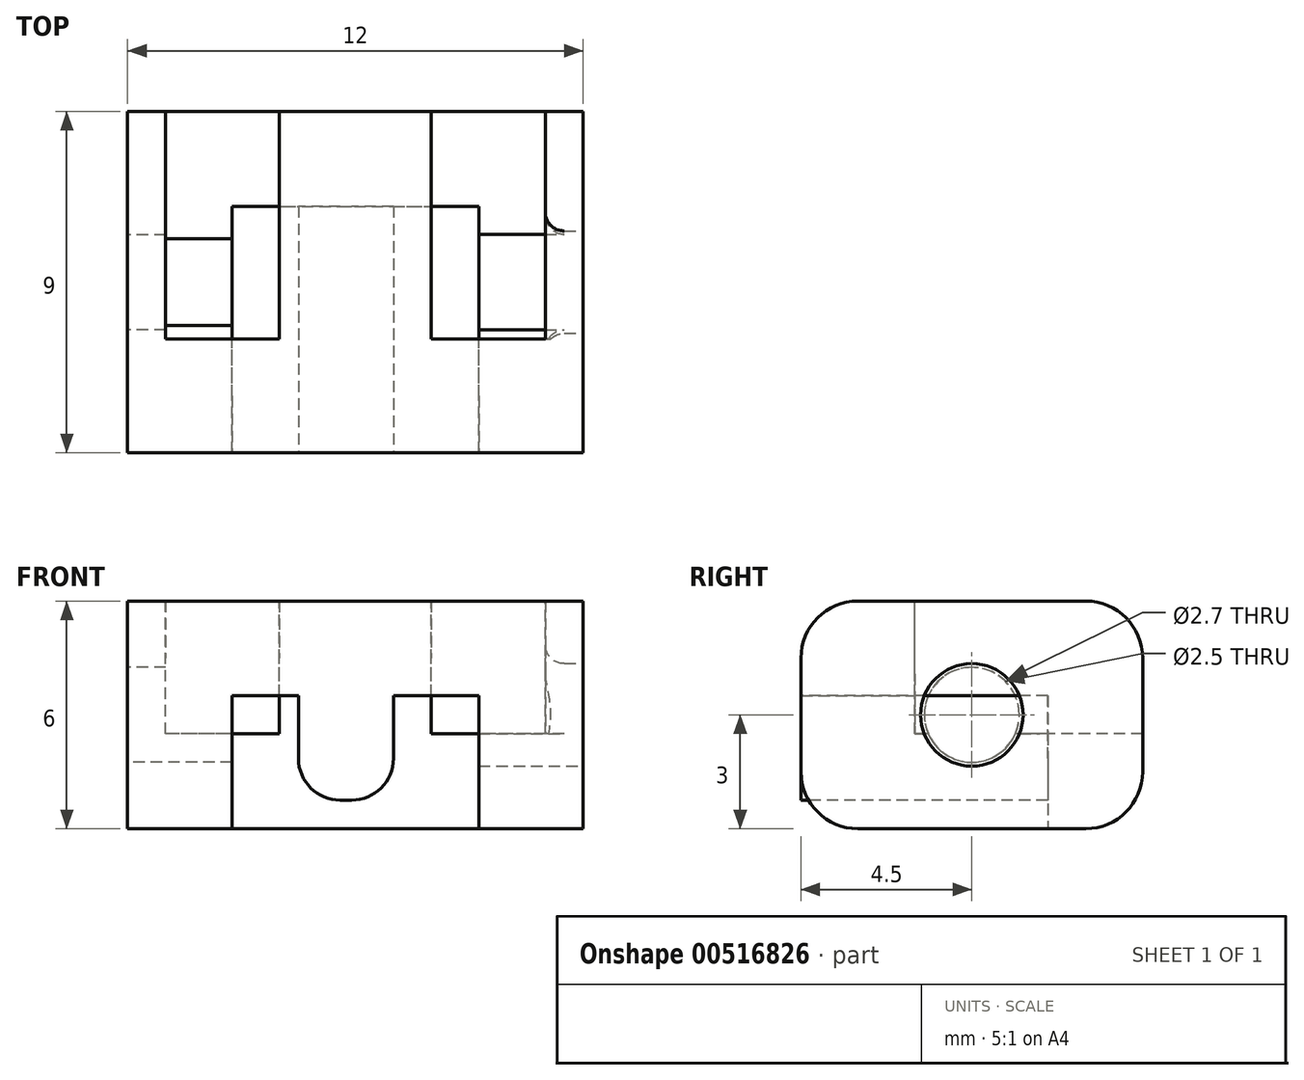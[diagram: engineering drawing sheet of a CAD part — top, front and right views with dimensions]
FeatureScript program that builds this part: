
annotation { "Feature Type Name" : "Feature", "Feature Type Description" : "" }
export const myFeature = defineFeature(function(context is Context, id is Id, definition is map)
    precondition{}
    {
        {
            var Q0;
            Q0=qCreatedBy(makeId("Top.planeOp"),FACE);
            var sketch = newSketch(context, id + "F0", { "sketchPlane" : qUnion([Q0])});
            skLineSegment(sketch, "E0.bottom", {"start": v(6, -4.5) * mm, "end": v(-6, -4.5) * mm});
            skLineSegment(sketch, "E0.top", {"start": v(6, 4.5) * mm, "end": v(-6, 4.5) * mm});
            skLineSegment(sketch, "E0.left", {"start": v(6, -4.5) * mm, "end": v(6, 4.5) * mm});
            skLineSegment(sketch, "E0.right", {"start": v(-6, -4.5) * mm, "end": v(-6, 4.5) * mm});
            skPoint(sketch, "E0.middle", {"position": v(0, 0) * mm});
            skSolve(sketch);
        }
        {
            var Q0;
            Q0=qSketchRegion(id+"F0",true);
            extrude(context, id + "F1", {"entities" : qUnion([Q0]), "depth" : 6 * mm, "offsetDistance" : 25 * mm});
        }
        {
            var Q0;
            Q0=makeQuery(id+"F1.opExtrude","CAP_FACE",FACE,{"disambiguationData":[OSD([sQuery(id+"F0.wireOp",EDGE,"E0.bottom"),sQuery(id+"F0.wireOp",EDGE,"E0.top"),sQuery(id+"F0.wireOp",EDGE,"E0.left"),sQuery(id+"F0.wireOp",EDGE,"E0.right")])],"isStart":false});
            var sketch = newSketch(context, id + "F2", { "sketchPlane" : qUnion([Q0])});
            skLineSegment(sketch, "E1.bottom", {"start": v(-5, 4.5) * mm, "end": v(-2, 4.5) * mm});
            skLineSegment(sketch, "E1.top", {"start": v(-5, -1.5) * mm, "end": v(-2, -1.5) * mm});
            skLineSegment(sketch, "E1.left", {"start": v(-5, 4.5) * mm, "end": v(-5, -1.5) * mm});
            skLineSegment(sketch, "E1.right", {"start": v(-2, 4.5) * mm, "end": v(-2, -1.5) * mm});
            skLineSegment(sketch, "E2.bottom", {"start": v(5, 4.5) * mm, "end": v(2, 4.5) * mm});
            skLineSegment(sketch, "E2.top", {"start": v(5, -1.5) * mm, "end": v(2, -1.5) * mm});
            skLineSegment(sketch, "E2.left", {"start": v(5, 4.5) * mm, "end": v(5, -1.5) * mm});
            skLineSegment(sketch, "E2.right", {"start": v(2, 4.5) * mm, "end": v(2, -1.5) * mm});
            skSolve(sketch);
        }
        {
            var Q0;
            Q0=makeQuery(id+"F2.imprint","IMPRINT",FACE,{"disambiguationData":[TD([[makeQuery(id+"F2.imprint","IMPRINT",EDGE,{"derivedFrom":sQuery(id+"F2.wireOp",EDGE,"E2.bottom")}),1.0]])]});
            var Q1;
            Q1=makeQuery(id+"F2.imprint","IMPRINT",FACE,{"disambiguationData":[TD([[makeQuery(id+"F2.imprint","IMPRINT",EDGE,{"derivedFrom":sQuery(id+"F2.wireOp",EDGE,"E1.bottom")}),1.0]])]});
            extrude(context, id + "F3", {"entities" : qUnion([Q0, Q1]), "operationType" : NewBodyOperationType.REMOVE, "oppositeDirection" : true, "depth" : 3.5 * mm, "offsetDistance" : 25 * mm});
        }
        {
            var Q0;
            Q0=makeQuery(id+"F1.opExtrude","CAP_FACE",FACE,{"disambiguationData":[OSD([sQuery(id+"F0.wireOp",EDGE,"E0.bottom"),sQuery(id+"F0.wireOp",EDGE,"E0.top"),sQuery(id+"F0.wireOp",EDGE,"E0.left"),sQuery(id+"F0.wireOp",EDGE,"E0.right")])],"isStart":true});
            var sketch = newSketch(context, id + "F4", { "sketchPlane" : qUnion([Q0])});
            skLineSegment(sketch, "E3.bottom", {"start": v(-3.25, 4.5) * mm, "end": v(3.25, 4.5) * mm});
            skLineSegment(sketch, "E3.top", {"start": v(-3.25, -2) * mm, "end": v(3.25, -2) * mm});
            skLineSegment(sketch, "E3.left", {"start": v(-3.25, 4.5) * mm, "end": v(-3.25, -2) * mm});
            skLineSegment(sketch, "E3.right", {"start": v(3.25, 4.5) * mm, "end": v(3.25, -2) * mm});
            skSolve(sketch);
        }
        {
            var Q0;
            Q0=qSketchRegion(id+"F4",true);
            extrude(context, id + "F5", {"entities" : qUnion([Q0]), "operationType" : NewBodyOperationType.REMOVE, "oppositeDirection" : true, "depth" : 3.5 * mm, "offsetDistance" : 25 * mm});
        }
        {
            var Q0;
            Q0=makeQuery(id+"F1.opExtrude","SWEPT_FACE",FACE,{"disambiguationData":[OSD([sQuery(id+"F0.wireOp",EDGE,"E0.left")])]});
            var sketch = newSketch(context, id + "F6", { "sketchPlane" : qUnion([Q0])});
            skLineSegment(sketch, "E4", {"start": v(0, 6) * mm, "end": v(0, 0) * mm, "construction": true});
            skLineSegment(sketch, "E5", {"start": v(-4.5, 3) * mm, "end": v(4.5, 3) * mm, "construction": true});
            skCircle(sketch, "E6", {"center": v(0, 3) * mm, "radius": 1.35 * mm});
            skSolve(sketch);
        }
        {
            var Q0;
            Q0=qSketchRegion(id+"F6",true);
            extrude(context, id + "F7", {"entities" : qUnion([Q0]), "operationType" : NewBodyOperationType.REMOVE, "oppositeDirection" : true, "depth" : 3 * mm, "offsetDistance" : 25 * mm});
        }
        {
            var Q0;
            Q0=makeQuery(id+"F1.opExtrude","SWEPT_FACE",FACE,{"disambiguationData":[OSD([sQuery(id+"F0.wireOp",EDGE,"E0.right")])]});
            var sketch = newSketch(context, id + "F8", { "sketchPlane" : qUnion([Q0])});
            skLineSegment(sketch, "E7", {"start": v(-4.5, 3) * mm, "end": v(4.5, 3) * mm, "construction": true});
            skLineSegment(sketch, "E8", {"start": v(0, 6) * mm, "end": v(0, 0) * mm, "construction": true});
            skCircle(sketch, "E9", {"center": v(0, 3) * mm, "radius": 1.25 * mm});
            skSolve(sketch);
        }
        {
            var Q0;
            Q0=qSketchRegion(id+"F8",true);
            extrude(context, id + "F9", {"entities" : qUnion([Q0]), "operationType" : NewBodyOperationType.REMOVE, "endBound" : BoundingType.UP_TO_NEXT, "oppositeDirection" : true, "depth" : 3 * mm, "offsetDistance" : 25 * mm});
        }
        {
            var Q0;
            Q0=makeQuery(id+"F3.boolean.opBoolean","COPY",EDGE,{"derivedFrom":makeQuery(id+"F3.opExtrude","CAP_EDGE",EDGE,{"disambiguationData":[OSD([sQuery(id+"F2.wireOp",EDGE,"E2.right")])],"isStart":true})});
            var Q1;
            Q1=makeQuery(id+"F3.boolean.opBoolean","COPY",EDGE,{"derivedFrom":makeQuery(id+"F3.opExtrude","CAP_EDGE",EDGE,{"disambiguationData":[OSD([sQuery(id+"F2.wireOp",EDGE,"E1.right")])],"isStart":true})});
            var Q2;
            Q2=makeQuery(id+"F1.opExtrude","CAP_EDGE",EDGE,{"disambiguationData":[OSD([sQuery(id+"F0.wireOp",EDGE,"E0.bottom")])],"isStart":false});
            var Q3;
            {var subQ0=sQuery(id+"F0.wireOp",EDGE,"E0.bottom");var subQ1=sQuery(id+"F0.wireOp",EDGE,"E0.right");Q3=makeQuery(id+"F5.boolean.opBoolean","SPLIT",EDGE,{"disambiguationData":[TD([makeQuery(id+"F1.opExtrude","SWEPT_FACE",FACE,{"disambiguationData":[OSD([subQ1])]})])],"derivedFrom":makeQuery(id+"F1.opExtrude","CAP_EDGE",EDGE,{"disambiguationData":[OSD([subQ0])],"isStart":true})});}
            var Q4;
            {var subQ0=sQuery(id+"F0.wireOp",EDGE,"E0.bottom");var subQ1=sQuery(id+"F0.wireOp",EDGE,"E0.left");Q4=makeQuery(id+"F5.boolean.opBoolean","SPLIT",EDGE,{"disambiguationData":[TD([makeQuery(id+"F1.opExtrude","SWEPT_FACE",FACE,{"disambiguationData":[OSD([subQ1])]})])],"derivedFrom":makeQuery(id+"F1.opExtrude","CAP_EDGE",EDGE,{"disambiguationData":[OSD([subQ0])],"isStart":true})});}
            var Q5;
            Q5=makeQuery(id+"F1.opExtrude","CAP_EDGE",EDGE,{"disambiguationData":[OSD([sQuery(id+"F0.wireOp",EDGE,"E0.top")])],"isStart":true});
            var Q6;
            {var subQ0=sQuery(id+"F0.wireOp",EDGE,"E0.right");var subQ1=sQuery(id+"F0.wireOp",EDGE,"E0.top");Q6=makeQuery(id+"F3.boolean.opBoolean","SPLIT",EDGE,{"disambiguationData":[TD([makeQuery(id+"F1.opExtrude","SWEPT_FACE",FACE,{"disambiguationData":[OSD([subQ0])]})])],"derivedFrom":makeQuery(id+"F1.opExtrude","CAP_EDGE",EDGE,{"disambiguationData":[OSD([subQ1])],"isStart":false})});}
            var Q7;
            {var subQ0=sQuery(id+"F0.wireOp",EDGE,"E0.left");var subQ1=sQuery(id+"F0.wireOp",EDGE,"E0.top");Q7=makeQuery(id+"F3.boolean.opBoolean","SPLIT",EDGE,{"disambiguationData":[TD([makeQuery(id+"F1.opExtrude","SWEPT_FACE",FACE,{"disambiguationData":[OSD([subQ0])]})])],"derivedFrom":makeQuery(id+"F1.opExtrude","CAP_EDGE",EDGE,{"disambiguationData":[OSD([subQ1])],"isStart":false})});}
            var Q8;
            {var subQ0=sQuery(id+"F0.wireOp",EDGE,"E0.top");Q8=makeQuery(id+"F3.boolean.opBoolean","SPLIT",EDGE,{"disambiguationData":[TD([makeQuery(id+"F3.opExtrude","SWEPT_FACE",FACE,{"disambiguationData":[OSD([sQuery(id+"F2.wireOp",EDGE,"E1.right")])]})])],"derivedFrom":makeQuery(id+"F1.opExtrude","CAP_EDGE",EDGE,{"disambiguationData":[OSD([subQ0])],"isStart":false})});}
            fillet(context, id + "F10", {"entities" : qUnion([Q0, Q1, Q2, Q3, Q4, Q5, Q6, Q7, Q8]), "radius" : 1.5 * mm, "tangentPropagation" : true, "allowEdgeOverflow" : false});
        }
        {
            var Q0;
            Q0=makeQuery(id+"F5.boolean.opBoolean","COPY",FACE,{"derivedFrom":makeQuery(id+"F5.opExtrude","CAP_FACE",FACE,{"disambiguationData":[OSD([sQuery(id+"F4.wireOp",EDGE,"E3.bottom"),sQuery(id+"F4.wireOp",EDGE,"E3.top"),sQuery(id+"F4.wireOp",EDGE,"E3.left"),sQuery(id+"F4.wireOp",EDGE,"E3.right")])],"isStart":false})});
            var sketch = newSketch(context, id + "F11", { "sketchPlane" : qUnion([Q0])});
            skLineSegment(sketch, "E10.bottom", {"start": v(-1.5, -2) * mm, "end": v(1, -2) * mm});
            skLineSegment(sketch, "E10.top", {"start": v(-1.5, 4.5) * mm, "end": v(1, 4.5) * mm});
            skLineSegment(sketch, "E10.left", {"start": v(-1.5, -2) * mm, "end": v(-1.5, 4.5) * mm});
            skLineSegment(sketch, "E10.right", {"start": v(1, -2) * mm, "end": v(1, 4.5) * mm});
            skSolve(sketch);
        }
        {
            var Q0;
            Q0=qSketchRegion(id+"F11",true);
            extrude(context, id + "F12", {"entities" : qUnion([Q0]), "operationType" : NewBodyOperationType.ADD, "depth" : 2.75 * mm, "offsetDistance" : 25 * mm});
        }
        {
            var Q0;
            Q0=makeQuery(id+"F12.opExtrude","CAP_EDGE",EDGE,{"disambiguationData":[OSD([sQuery(id+"F11.wireOp",EDGE,"E10.left")])],"isStart":false});
            var Q1;
            Q1=makeQuery(id+"F12.opExtrude","CAP_EDGE",EDGE,{"disambiguationData":[OSD([sQuery(id+"F11.wireOp",EDGE,"E10.right")])],"isStart":false});
            fillet(context, id + "F13", {"entities" : qUnion([Q0, Q1]), "radius" : 1.1 * mm, "tangentPropagation" : true, "allowEdgeOverflow" : false});
        }
        {
            var Q0;
            Q0=makeQuery(id+"F7.boolean.opBoolean","COPY",EDGE,{"derivedFrom":makeQuery(id+"F7.opExtrude","CAP_EDGE",EDGE,{"disambiguationData":[OSD([sQuery(id+"F6.wireOp",EDGE,"E6")])],"isStart":true})});
            var Q1;
            Q1=makeQuery(id+"F9.boolean.opBoolean","COPY",EDGE,{"derivedFrom":makeQuery(id+"F9.opExtrude","CAP_EDGE",EDGE,{"disambiguationData":[OSD([sQuery(id+"F8.wireOp",EDGE,"E9")])],"isStart":true})});
            var Q2;
            Q2=makeQuery(id+"F9.boolean.opBoolean","COPY",EDGE,{"derivedFrom":makeQuery(id+"F9.opExtrude","CAP_EDGE",EDGE,{"disambiguationData":[OSD([sQuery(id+"F8.wireOp",EDGE,"E9")]),topologyDisambiguationEdgeConnected([makeQuery(id+"F3.boolean.opBoolean","COPY",FACE,{"derivedFrom":makeQuery(id+"F3.opExtrude","SWEPT_FACE",FACE,{"disambiguationData":[OSD([sQuery(id+"F2.wireOp",EDGE,"E1.left")])]})})])],"isStart":false})});
            var Q3;
            Q3=makeQuery(id+"F7.boolean.opBoolean","INTERSECT",EDGE,{"derivedFrom":[makeQuery(id+"F3.boolean.opBoolean","COPY",FACE,{"derivedFrom":makeQuery(id+"F3.opExtrude","SWEPT_FACE",FACE,{"disambiguationData":[OSD([sQuery(id+"F2.wireOp",EDGE,"E2.left")])]})}),makeQuery(id+"F7.opExtrude","SWEPT_FACE",FACE,{"disambiguationData":[OSD([sQuery(id+"F6.wireOp",EDGE,"E6")])]})]});
            var Q4;
            Q4=makeQuery(id+"F7.boolean.opBoolean","COPY",EDGE,{"derivedFrom":makeQuery(id+"F7.opExtrude","CAP_EDGE",EDGE,{"disambiguationData":[OSD([sQuery(id+"F6.wireOp",EDGE,"E6")])],"isStart":false})});
            var Q5;
            Q5=makeQuery(id+"F9.boolean.opBoolean","COPY",EDGE,{"derivedFrom":makeQuery(id+"F9.opExtrude","CAP_EDGE",EDGE,{"disambiguationData":[OSD([sQuery(id+"F8.wireOp",EDGE,"E9")]),topologyDisambiguationEdgeConnected([makeQuery(id+"F5.boolean.opBoolean","COPY",FACE,{"derivedFrom":makeQuery(id+"F5.opExtrude","SWEPT_FACE",FACE,{"disambiguationData":[OSD([sQuery(id+"F4.wireOp",EDGE,"E3.left")])]})})])],"isStart":false})});
            fillet(context, id + "F14", {"entities" : qUnion([Q0, Q1, Q2, Q3, Q4, Q5]), "radius" : .5 * mm, "tangentPropagation" : true, "allowEdgeOverflow" : false});
        }
    });
